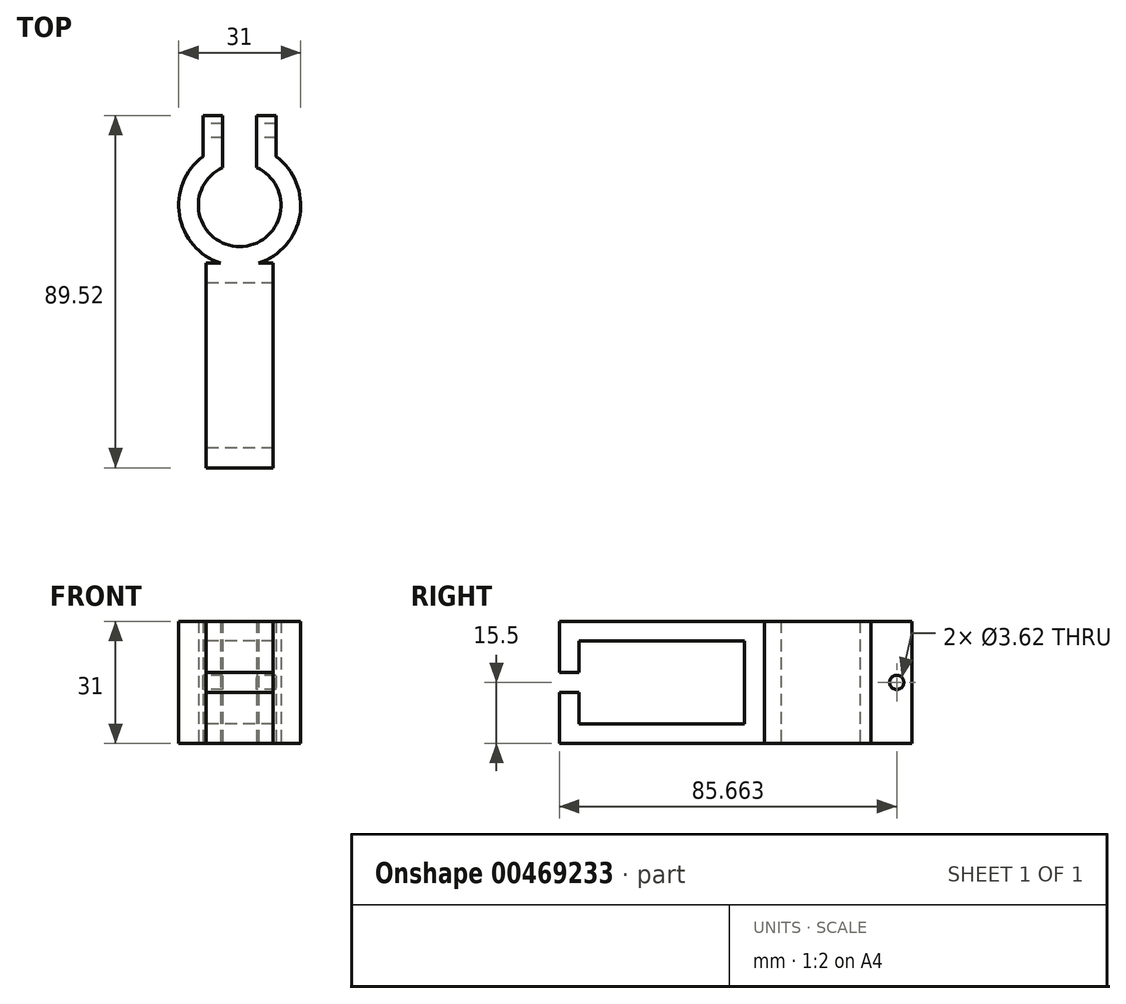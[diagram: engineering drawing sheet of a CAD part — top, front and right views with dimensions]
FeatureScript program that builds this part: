
annotation { "Feature Type Name" : "Feature", "Feature Type Description" : "" }
export const myFeature = defineFeature(function(context is Context, id is Id, definition is map)
    precondition{}
    {
        {
            var Q0;
            Q0=qCreatedBy(makeId("Top.planeOp"),FACE);
            var sketch = newSketch(context, id + "F0", { "sketchPlane" : qUnion([Q0])});
            skLineSegment(sketch, "E0", {"start": v(-4.31, 43.79) * mm, "end": v(-4.31, 30.57) * mm});
            skLineSegment(sketch, "E1", {"start": v(7, -45.73) * mm, "end": v(-8.5, -45.73) * mm});
            skLineSegment(sketch, "E2", {"start": v(-8.5, -45.73) * mm, "end": v(-8.5, 6.27) * mm});
            skLineSegment(sketch, "E3", {"start": v(-8.5, 6.27) * mm, "end": v(-4.84, 6.27) * mm});
            skLineSegment(sketch, "E4", {"start": v(-4.31, 43.79) * mm, "end": v(-9.31, 43.79) * mm});
            skLineSegment(sketch, "E5", {"start": v(-9.31, 43.79) * mm, "end": v(-9.31, 33.4) * mm});
            skArc(sketch, "E6", {"start": v(-4.31, 30.57) * mm, "mid": v(-10.14, 18.26) * mm, "end": v(1.1, 10.56) * mm});
            skArc(sketch, "E7", {"start": v(-9.31, 33.4) * mm, "mid": v(-15.3, 18.48) * mm, "end": v(-4.84, 6.27) * mm});
            skLineSegment(sketch, "E8", {"start": v(0, 39.1) * mm, "end": v(0, 10.5) * mm});
            skArc(sketch, "E9.MirrorCS", {"start": v(9.31, 33.4) * mm, "mid": v(15.3, 18.48) * mm, "end": v(4.84, 6.27) * mm});
            skArc(sketch, "E10.MirrorCS", {"start": v(4.31, 30.57) * mm, "mid": v(10.14, 18.26) * mm, "end": v(-1.1, 10.56) * mm});
            skLineSegment(sketch, "E11.MirrorCS", {"start": v(4.31, 43.79) * mm, "end": v(4.31, 30.57) * mm});
            skLineSegment(sketch, "E12.MirrorCS", {"start": v(9.31, 43.79) * mm, "end": v(9.31, 33.4) * mm});
            skLineSegment(sketch, "E13.MirrorCS", {"start": v(4.31, 43.79) * mm, "end": v(9.31, 43.79) * mm});
            skLineSegment(sketch, "E14.MirrorCS", {"start": v(8.5, 6.27) * mm, "end": v(4.84, 6.27) * mm});
            skLineSegment(sketch, "E15.MirrorCS", {"start": v(8.5, -45.73) * mm, "end": v(8.5, 6.27) * mm});
            skLineSegment(sketch, "E16.MirrorCS", {"start": v(-7, -45.73) * mm, "end": v(8.5, -45.73) * mm});
            skSolve(sketch);
        }
        {
            var Q0;
            Q0=makeQuery(id+"F0.imprint","IMPRINT",FACE,{"disambiguationData":[TD([[makeQuery(id+"F0.imprint","IMPRINT",EDGE,{"derivedFrom":sQuery(id+"F0.wireOp",EDGE,"E0")}),-1.0]])]});
            var Q1;
            Q1=makeQuery(id+"F0.imprint","IMPRINT",FACE,{"disambiguationData":[TD([[makeQuery(id+"F0.imprint","IMPRINT",EDGE,{"derivedFrom":sQuery(id+"F0.wireOp",EDGE,"E9.MirrorCS")}),-1.0]])]});
            extrude(context, id + "F1", {"entities" : qUnion([Q0, Q1]), "depth" : 31 * mm});
        }
        {
            var Q0;
            Q0=makeQuery(id+"F1.opExtrude","SWEPT_FACE",FACE,{"disambiguationData":[OSD([sQuery(id+"F0.wireOp",EDGE,"E5")])]});
            var sketch = newSketch(context, id + "F2", { "sketchPlane" : qUnion([Q0])});
            skCircle(sketch, "E17", {"center": v(-39.93, 15.5) * mm, "radius": 1.8 * mm});
            skPoint(sketch, "E17.centerSnap0", {"position": v(-43.79, 15.5) * mm});
            skSolve(sketch);
        }
        {
            var Q0;
            Q0 = qSketchRegion(id + "F2", true);
            extrude(context, id + "F3", {"entities" : qUnion([Q0]), "operationType" : NewBodyOperationType.REMOVE, "oppositeDirection" : true, "depth" : 25 * mm});
        }
        {
            var Q0;
            Q0=makeQuery(id+"F1.opExtrude","SWEPT_FACE",FACE,{"disambiguationData":[OSD([sQuery(id+"F0.wireOp",EDGE,"E2")])]});
            var sketch = newSketch(context, id + "F4", { "sketchPlane" : qUnion([Q0])});
            skLineSegment(sketch, "E18", {"start": v(40.73, 13) * mm, "end": v(40.73, 5) * mm});
            skLineSegment(sketch, "E19", {"start": v(40.73, 5) * mm, "end": v(-1.27, 5) * mm});
            skLineSegment(sketch, "E20", {"start": v(-1.27, 5) * mm, "end": v(-1.27, 26) * mm});
            skLineSegment(sketch, "E21", {"start": v(-1.27, 26) * mm, "end": v(40.73, 26) * mm});
            skLineSegment(sketch, "E22", {"start": v(40.73, 26) * mm, "end": v(40.73, 18) * mm});
            skLineSegment(sketch, "E23", {"start": v(40.73, 18) * mm, "end": v(45.73, 18) * mm});
            skLineSegment(sketch, "E24", {"start": v(45.73, 18) * mm, "end": v(45.73, 13) * mm});
            skLineSegment(sketch, "E25", {"start": v(45.73, 13) * mm, "end": v(40.73, 13) * mm});
            skLineSegment(sketch, "E26", {"start": v(45.73, 18) * mm, "end": v(45.73, 31) * mm});
            skLineSegment(sketch, "E27", {"start": v(45.73, 13) * mm, "end": v(45.73, 0) * mm});
            skSolve(sketch);
        }
        {
            var Q0;
            Q0=makeQuery(id+"F4.imprint","IMPRINT",FACE,{"disambiguationData":[TD([[makeQuery(id+"F4.imprint","IMPRINT",EDGE,{"derivedFrom":sQuery(id+"F4.wireOp",EDGE,"E18")}),-1.0]])]});
            extrude(context, id + "F5", {"entities" : qUnion([Q0]), "operationType" : NewBodyOperationType.REMOVE, "oppositeDirection" : true, "depth" : 25 * mm});
        }
    });
